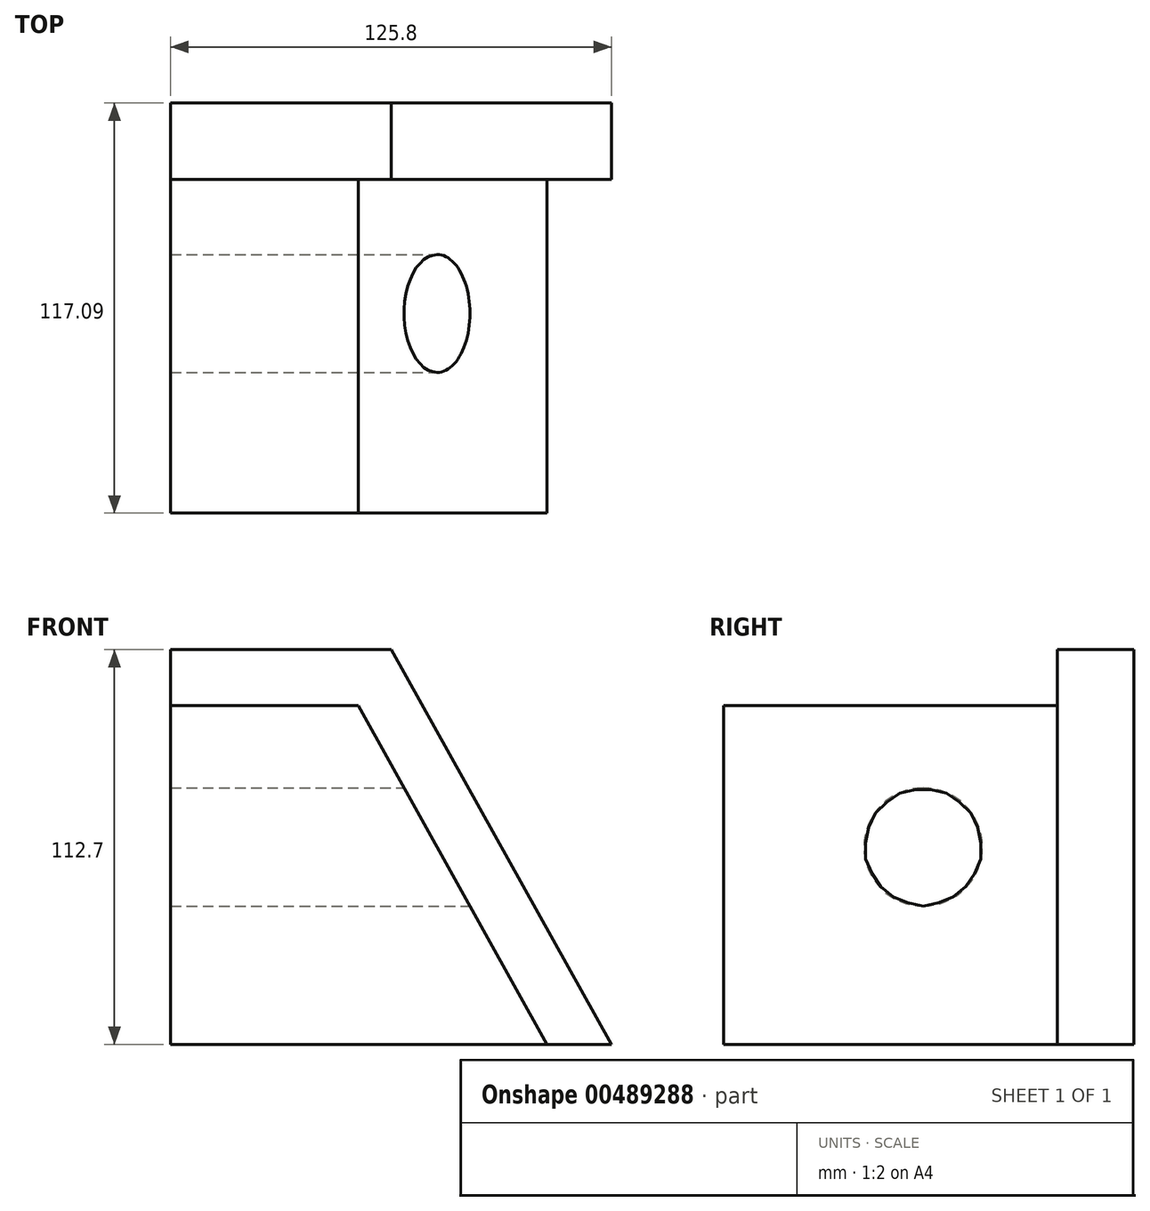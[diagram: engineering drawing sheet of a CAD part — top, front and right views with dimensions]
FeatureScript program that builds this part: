
annotation { "Feature Type Name" : "Feature", "Feature Type Description" : "" }
export const myFeature = defineFeature(function(context is Context, id is Id, definition is map)
    precondition{}
    {
        {
            var Q0;
            Q0=qCreatedBy(makeId("Front.planeOp"),FACE);
            var sketch = newSketch(context, id + "F0", { "sketchPlane" : qUnion([Q0])});
            skLineSegment(sketch, "E0.bottom", {"start": v(0, 56.35) * mm, "end": v(-62.9, 56.35) * mm});
            skLineSegment(sketch, "E0.top", {"start": v(62.9, -56.35) * mm, "end": v(-62.9, -56.35) * mm});
            skLineSegment(sketch, "E0.right", {"start": v(-62.9, 56.35) * mm, "end": v(-62.9, -56.35) * mm});
            skPoint(sketch, "E0.middle", {"position": v(0, 0) * mm});
            skLineSegment(sketch, "E1", {"start": v(62.9, -56.35) * mm, "end": v(0, 56.35) * mm});
            skLineSegment(sketch, "E2.0", {"start": v(-9.4, 40.34) * mm, "end": v(-62.9, 40.34) * mm});
            skLineSegment(sketch, "E2.1", {"start": v(44.57, -56.35) * mm, "end": v(-9.4, 40.34) * mm});
            skSolve(sketch);
        }
        {
            var Q0;
            {var subQ1=sQuery(id+"F0.wireOp",EDGE,"E0.bottom");Q0=makeQuery(id+"F0.imprint","IMPRINT",FACE,{"disambiguationData":[TD([[makeQuery(id+"F0.imprint","IMPRINT",EDGE,{"derivedFrom":subQ1}),1.0]])]});}
            var Q1;
            {var subQ4=sQuery(id+"F0.wireOp",EDGE,"E2.0");Q1=makeQuery(id+"F0.imprint","IMPRINT",FACE,{"disambiguationData":[TD([[makeQuery(id+"F0.imprint","IMPRINT",EDGE,{"derivedFrom":subQ4}),1.0]])]});}
            extrude(context, id + "F1", {"entities" : qUnion([Q0, Q1]), "oppositeDirection" : true, "depth" : 21.84 * mm});
        }
        {
            var Q0;
            {var subQ4=sQuery(id+"F0.wireOp",EDGE,"E2.0");Q0=makeQuery(id+"F0.imprint","IMPRINT",FACE,{"disambiguationData":[TD([[makeQuery(id+"F0.imprint","IMPRINT",EDGE,{"derivedFrom":subQ4}),1.0]])]});}
            extrude(context, id + "F2", {"entities" : qUnion([Q0]), "operationType" : NewBodyOperationType.ADD, "depth" : 95.25 * mm});
        }
        {
            var Q0;
            Q0=qCreatedBy(makeId("Right.planeOp"),FACE);
            var sketch = newSketch(context, id + "F3", { "sketchPlane" : qUnion([Q0])});
            skCircle(sketch, "E3", {"center": v(-38.25, 0) * mm, "radius": 16.87 * mm});
            skSolve(sketch);
        }
        {
            var Q0;
            Q0 = qSketchRegion(id + "F3", true);
            extrude(context, id + "F4", {"entities" : qUnion([Q0]), "operationType" : NewBodyOperationType.REMOVE, "endBound" : BoundingType.SYMMETRIC, "oppositeDirection" : true, "depth" : 127 * mm});
        }
    });
